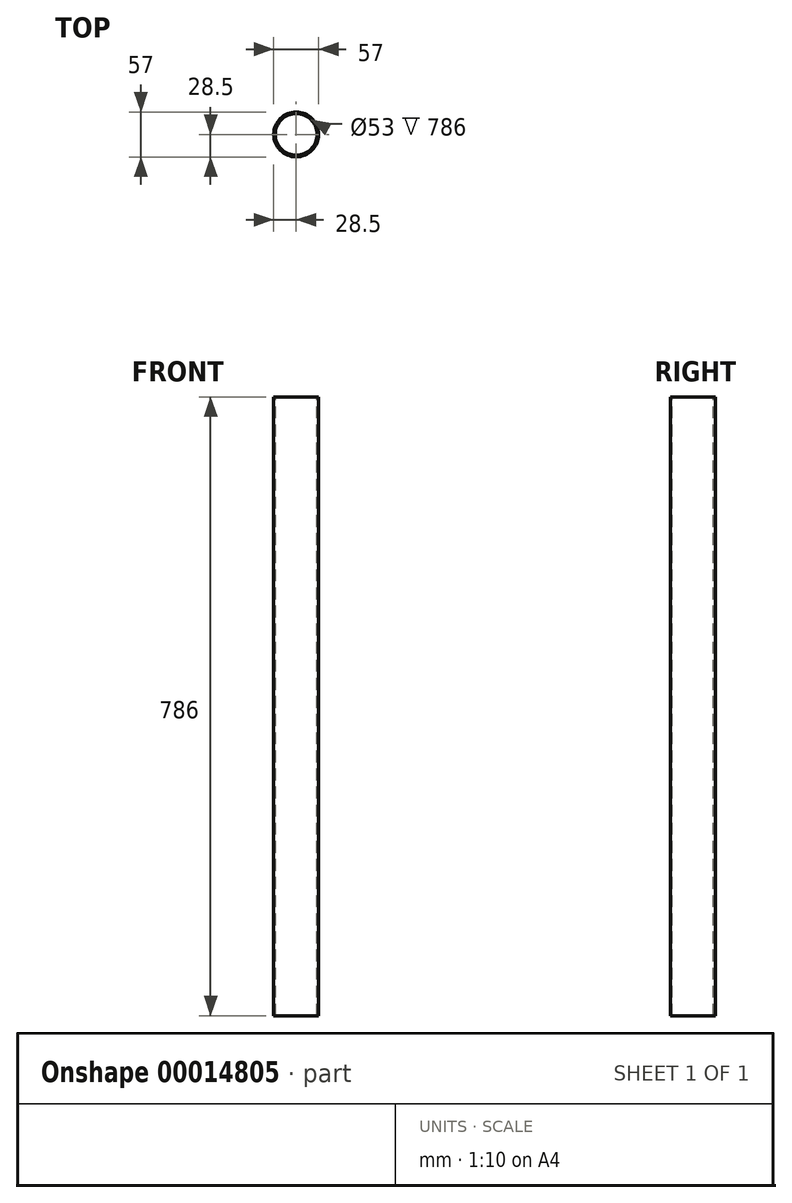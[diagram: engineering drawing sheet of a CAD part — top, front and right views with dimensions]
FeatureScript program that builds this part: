
annotation { "Feature Type Name" : "Feature", "Feature Type Description" : "" }
export const myFeature = defineFeature(function(context is Context, id is Id, definition is map)
    precondition{}
    {
        {
            var Q0;
            Q0=qCreatedBy(makeId("Top.planeOp"),FACE);
            var sketch = newSketch(context, id + "F0", { "sketchPlane" : qUnion([Q0])});
            skCircle(sketch, "E0", {"center": v(0, 0) * mm, "radius": 26.5 * mm});
            skCircle(sketch, "E1", {"center": v(0, 0) * mm, "radius": 28.5 * mm});
            skSolve(sketch);
        }
        {
            var Q0;
            Q0=makeQuery(id+"F0.imprint","IMPRINT",FACE,{"disambiguationData":[TD([[makeQuery(id+"F0.imprint","IMPRINT",EDGE,{"derivedFrom":sQuery(id+"F0.wireOp",EDGE,"E0")}),-1.0]])]});
            extrude(context, id + "F1", {"entities" : qUnion([Q0]), "oppositeDirection" : true, "depth" : 786 * mm});
        }
    });
